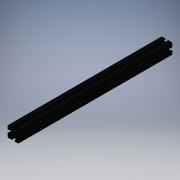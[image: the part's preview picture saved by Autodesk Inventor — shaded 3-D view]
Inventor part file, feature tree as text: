
AUTODESK INVENTOR PART (.ipt)
format: ipt  version: 2019 (Build 230136000, 136)  size: 260,608 bytes
history: native  units: in
note: dims shown in document units (in); Inventor stores cm internally (conversion verified against a paired STEP export)
features: plane x1, extrude x1, sketch x1
ambient origin geometry x8: Origin, YZ Plane, XZ Plane, XY Plane, X Axis, Y Axis, Z Axis, Center Point
bodies: Solid1 (feature_tree)
feature tree (3):
  plane  "Work Plane1"
  extrude  "Extrusion1"  [1 undecoded]
  sketch  "Sketch1"  dims[d0=20.625in d1=0.0in]
note: 1 required parameter value undecoded (feature->parameter linkage not recoverable at this tier; creation-order binding heuristic only, values carry confidence <= 0.55)
